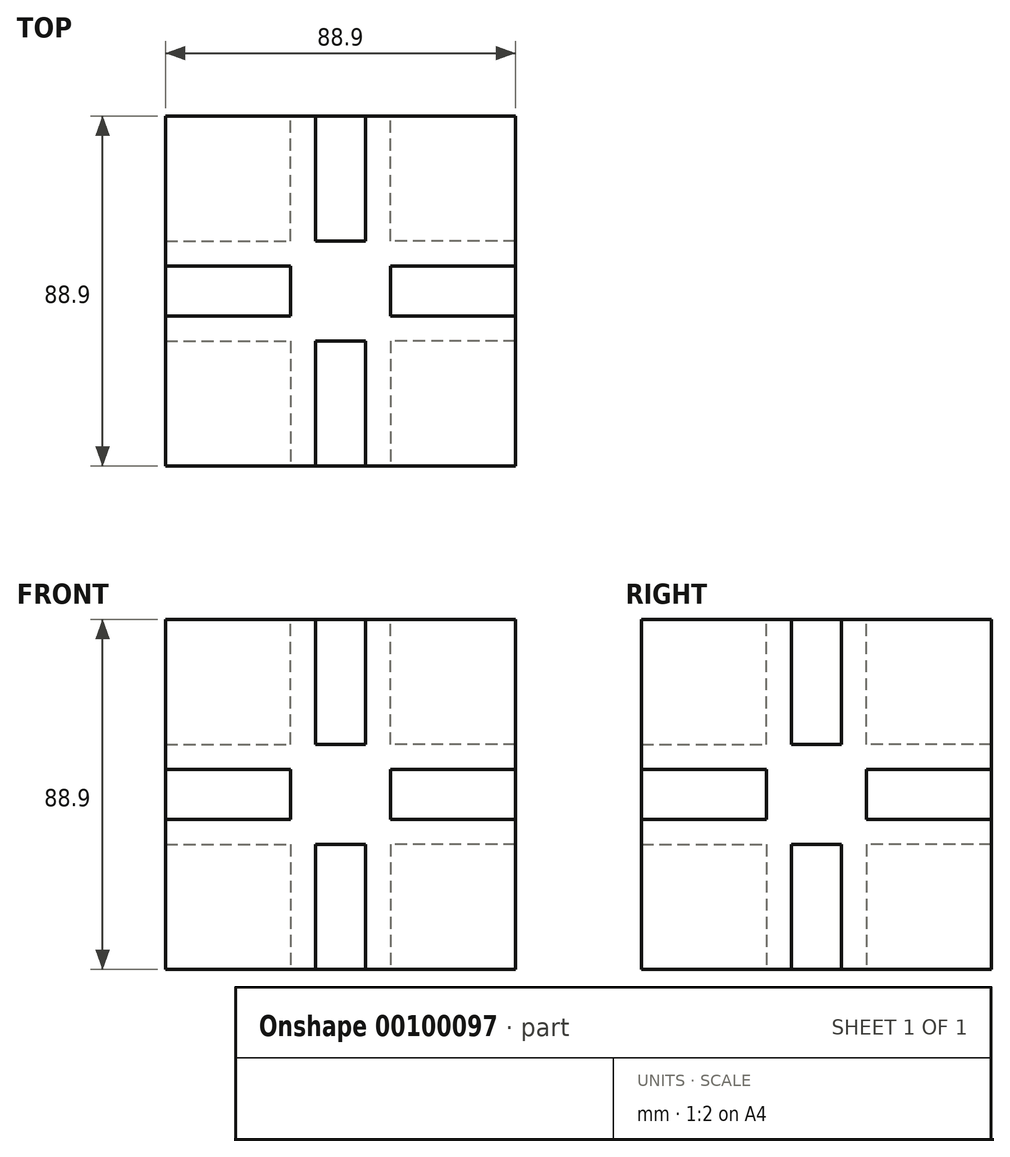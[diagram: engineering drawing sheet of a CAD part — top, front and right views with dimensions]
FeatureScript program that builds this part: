
annotation { "Feature Type Name" : "Feature", "Feature Type Description" : "" }
export const myFeature = defineFeature(function(context is Context, id is Id, definition is map)
    precondition{}
    {
        {
            var Q0;
            Q0=qCreatedBy(makeId("Top.planeOp"),FACE);
            var sketch = newSketch(context, id + "F0", { "sketchPlane" : qUnion([Q0])});
            skLineSegment(sketch, "E0.bottom", {"start": v(-44.45, 44.45) * mm, "end": v(44.45, 44.45) * mm});
            skLineSegment(sketch, "E0.top", {"start": v(-44.45, -44.45) * mm, "end": v(44.45, -44.45) * mm});
            skLineSegment(sketch, "E0.left", {"start": v(-44.45, 44.45) * mm, "end": v(-44.45, -44.45) * mm});
            skLineSegment(sketch, "E0.right", {"start": v(44.45, 44.45) * mm, "end": v(44.45, -44.45) * mm});
            skSolve(sketch);
        }
        {
            var Q0;
            Q0 = qSketchRegion(id + "F0", true);
            extrude(context, id + "F1", {"entities" : qUnion([Q0]), "endBound" : BoundingType.SYMMETRIC, "depth" : 88.9 * mm});
        }
        {
            var Q0;
            Q0=makeQuery(id+"F1.opExtrude","CAP_FACE",FACE,{"disambiguationData":[OSD([sQuery(id+"F0.wireOp",EDGE,"E0.bottom"),sQuery(id+"F0.wireOp",EDGE,"E0.top"),sQuery(id+"F0.wireOp",EDGE,"E0.left"),sQuery(id+"F0.wireOp",EDGE,"E0.right")])],"isStart":false});
            var sketch = newSketch(context, id + "F2", { "sketchPlane" : qUnion([Q0])});
            skLineSegment(sketch, "E1.bottom", {"start": v(48.2, 6.35) * mm, "end": v(12.7, 6.35) * mm});
            skLineSegment(sketch, "E1.top", {"start": v(48.2, -6.35) * mm, "end": v(12.7, -6.35) * mm});
            skLineSegment(sketch, "E1.left", {"start": v(48.2, 6.35) * mm, "end": v(48.2, -6.35) * mm});
            skLineSegment(sketch, "E1.right", {"start": v(12.7, 6.35) * mm, "end": v(12.7, -6.35) * mm});
            skLineSegment(sketch, "E2.bottom", {"start": v(6.35, -56.54) * mm, "end": v(-6.35, -56.54) * mm});
            skLineSegment(sketch, "E2.top", {"start": v(6.35, -12.7) * mm, "end": v(-6.35, -12.7) * mm});
            skLineSegment(sketch, "E2.left", {"start": v(6.35, -56.54) * mm, "end": v(6.35, -12.7) * mm});
            skLineSegment(sketch, "E2.right", {"start": v(-6.35, -56.54) * mm, "end": v(-6.35, -12.7) * mm});
            skLineSegment(sketch, "E3.bottom", {"start": v(-62.36, 6.35) * mm, "end": v(-12.7, 6.35) * mm});
            skLineSegment(sketch, "E3.top", {"start": v(-62.36, -6.35) * mm, "end": v(-12.7, -6.35) * mm});
            skLineSegment(sketch, "E3.left", {"start": v(-62.36, 6.35) * mm, "end": v(-62.36, -6.35) * mm});
            skLineSegment(sketch, "E3.right", {"start": v(-12.7, 6.35) * mm, "end": v(-12.7, -6.35) * mm});
            skLineSegment(sketch, "E4.bottom", {"start": v(6.35, 65.89) * mm, "end": v(-6.35, 65.89) * mm});
            skLineSegment(sketch, "E4.top", {"start": v(6.35, 12.7) * mm, "end": v(-6.35, 12.7) * mm});
            skLineSegment(sketch, "E4.left", {"start": v(6.35, 65.89) * mm, "end": v(6.35, 12.7) * mm});
            skLineSegment(sketch, "E4.right", {"start": v(-6.35, 65.89) * mm, "end": v(-6.35, 12.7) * mm});
            skSolve(sketch);
        }
        {
            var Q0;
            Q0 = qSketchRegion(id + "F2", true);
            extrude(context, id + "F3", {"entities" : qUnion([Q0]), "operationType" : NewBodyOperationType.REMOVE, "oppositeDirection" : true, "depth" : 31.75 * mm});
        }
        {
            var Q0;
            Q0=makeQuery(id+"F1.opExtrude","CAP_FACE",FACE,{"disambiguationData":[OSD([sQuery(id+"F0.wireOp",EDGE,"E0.bottom"),sQuery(id+"F0.wireOp",EDGE,"E0.top"),sQuery(id+"F0.wireOp",EDGE,"E0.left"),sQuery(id+"F0.wireOp",EDGE,"E0.right")])],"isStart":true});
            var sketch = newSketch(context, id + "F4", { "sketchPlane" : qUnion([Q0])});
            skLineSegment(sketch, "E5.bottom", {"start": v(56.23, 6.35) * mm, "end": v(12.7, 6.35) * mm});
            skLineSegment(sketch, "E5.top", {"start": v(56.23, -6.35) * mm, "end": v(12.7, -6.35) * mm});
            skLineSegment(sketch, "E5.left", {"start": v(56.23, 6.35) * mm, "end": v(56.23, -6.35) * mm});
            skLineSegment(sketch, "E5.right", {"start": v(12.7, 6.35) * mm, "end": v(12.7, -6.35) * mm});
            skLineSegment(sketch, "E6.1.0", {"start": v(-6.35, 56.23) * mm, "end": v(-6.35, 12.7) * mm});
            skLineSegment(sketch, "E6.1.1", {"start": v(-6.35, 56.23) * mm, "end": v(6.35, 56.23) * mm});
            skLineSegment(sketch, "E6.1.2", {"start": v(6.35, 56.23) * mm, "end": v(6.35, 12.7) * mm});
            skLineSegment(sketch, "E6.1.3", {"start": v(-6.35, 12.7) * mm, "end": v(6.35, 12.7) * mm});
            skLineSegment(sketch, "E6.2.0", {"start": v(-56.23, -6.35) * mm, "end": v(-12.7, -6.35) * mm});
            skLineSegment(sketch, "E6.2.1", {"start": v(-56.23, -6.35) * mm, "end": v(-56.23, 6.35) * mm});
            skLineSegment(sketch, "E6.2.2", {"start": v(-56.23, 6.35) * mm, "end": v(-12.7, 6.35) * mm});
            skLineSegment(sketch, "E6.2.3", {"start": v(-12.7, -6.35) * mm, "end": v(-12.7, 6.35) * mm});
            skLineSegment(sketch, "E6.3.0", {"start": v(6.35, -56.23) * mm, "end": v(6.35, -12.7) * mm});
            skLineSegment(sketch, "E6.3.1", {"start": v(6.35, -56.23) * mm, "end": v(-6.35, -56.23) * mm});
            skLineSegment(sketch, "E6.3.2", {"start": v(-6.35, -56.23) * mm, "end": v(-6.35, -12.7) * mm});
            skLineSegment(sketch, "E6.3.3", {"start": v(6.35, -12.7) * mm, "end": v(-6.35, -12.7) * mm});
            skPoint(sketch, "E6.center", {"position": v(0, 0) * mm});
            skSolve(sketch);
        }
        {
            var Q0;
            Q0 = qSketchRegion(id + "F4", true);
            extrude(context, id + "F5", {"entities" : qUnion([Q0]), "operationType" : NewBodyOperationType.REMOVE, "oppositeDirection" : true, "depth" : 31.75 * mm});
        }
        {
            var Q0;
            Q0=makeQuery(id+"F1.opExtrude","SWEPT_FACE",FACE,{"disambiguationData":[OSD([sQuery(id+"F0.wireOp",EDGE,"E0.top")])]});
            var sketch = newSketch(context, id + "F6", { "sketchPlane" : qUnion([Q0])});
            skLineSegment(sketch, "E7.bottom", {"start": v(52.44, -6.35) * mm, "end": v(12.7, -6.35) * mm});
            skLineSegment(sketch, "E7.top", {"start": v(52.44, 6.35) * mm, "end": v(12.7, 6.35) * mm});
            skLineSegment(sketch, "E7.left", {"start": v(52.44, -6.35) * mm, "end": v(52.44, 6.35) * mm});
            skLineSegment(sketch, "E7.right", {"start": v(12.7, -6.35) * mm, "end": v(12.7, 6.35) * mm});
            skLineSegment(sketch, "E8.bottom", {"start": v(-63.9, -6.35) * mm, "end": v(-12.7, -6.35) * mm});
            skLineSegment(sketch, "E8.top", {"start": v(-63.9, 6.35) * mm, "end": v(-12.7, 6.35) * mm});
            skLineSegment(sketch, "E8.left", {"start": v(-63.9, -6.35) * mm, "end": v(-63.9, 6.35) * mm});
            skLineSegment(sketch, "E8.right", {"start": v(-12.7, -6.35) * mm, "end": v(-12.7, 6.35) * mm});
            skSolve(sketch);
        }
        {
            var Q0;
            Q0 = qSketchRegion(id + "F6", true);
            extrude(context, id + "F7", {"entities" : qUnion([Q0]), "operationType" : NewBodyOperationType.REMOVE, "oppositeDirection" : true, "depth" : 31.75 * mm});
        }
        {
            var Q0;
            Q0=makeQuery(id+"F1.opExtrude","SWEPT_FACE",FACE,{"disambiguationData":[OSD([sQuery(id+"F0.wireOp",EDGE,"E0.bottom")])]});
            var sketch = newSketch(context, id + "F8", { "sketchPlane" : qUnion([Q0])});
            skLineSegment(sketch, "E9.bottom", {"start": v(51.86, -6.35) * mm, "end": v(12.7, -6.35) * mm});
            skLineSegment(sketch, "E9.top", {"start": v(51.86, 6.35) * mm, "end": v(12.7, 6.35) * mm});
            skLineSegment(sketch, "E9.left", {"start": v(51.86, -6.35) * mm, "end": v(51.86, 6.35) * mm});
            skLineSegment(sketch, "E9.right", {"start": v(12.7, -6.35) * mm, "end": v(12.7, 6.35) * mm});
            skLineSegment(sketch, "E10.bottom", {"start": v(-52.5, -6.35) * mm, "end": v(-12.7, -6.35) * mm});
            skLineSegment(sketch, "E10.top", {"start": v(-52.5, 6.35) * mm, "end": v(-12.7, 6.35) * mm});
            skLineSegment(sketch, "E10.left", {"start": v(-52.5, -6.35) * mm, "end": v(-52.5, 6.35) * mm});
            skLineSegment(sketch, "E10.right", {"start": v(-12.7, -6.35) * mm, "end": v(-12.7, 6.35) * mm});
            skSolve(sketch);
        }
        {
            var Q0;
            Q0 = qSketchRegion(id + "F8", true);
            extrude(context, id + "F9", {"entities" : qUnion([Q0]), "operationType" : NewBodyOperationType.REMOVE, "oppositeDirection" : true, "depth" : 31.75 * mm});
        }
    });
